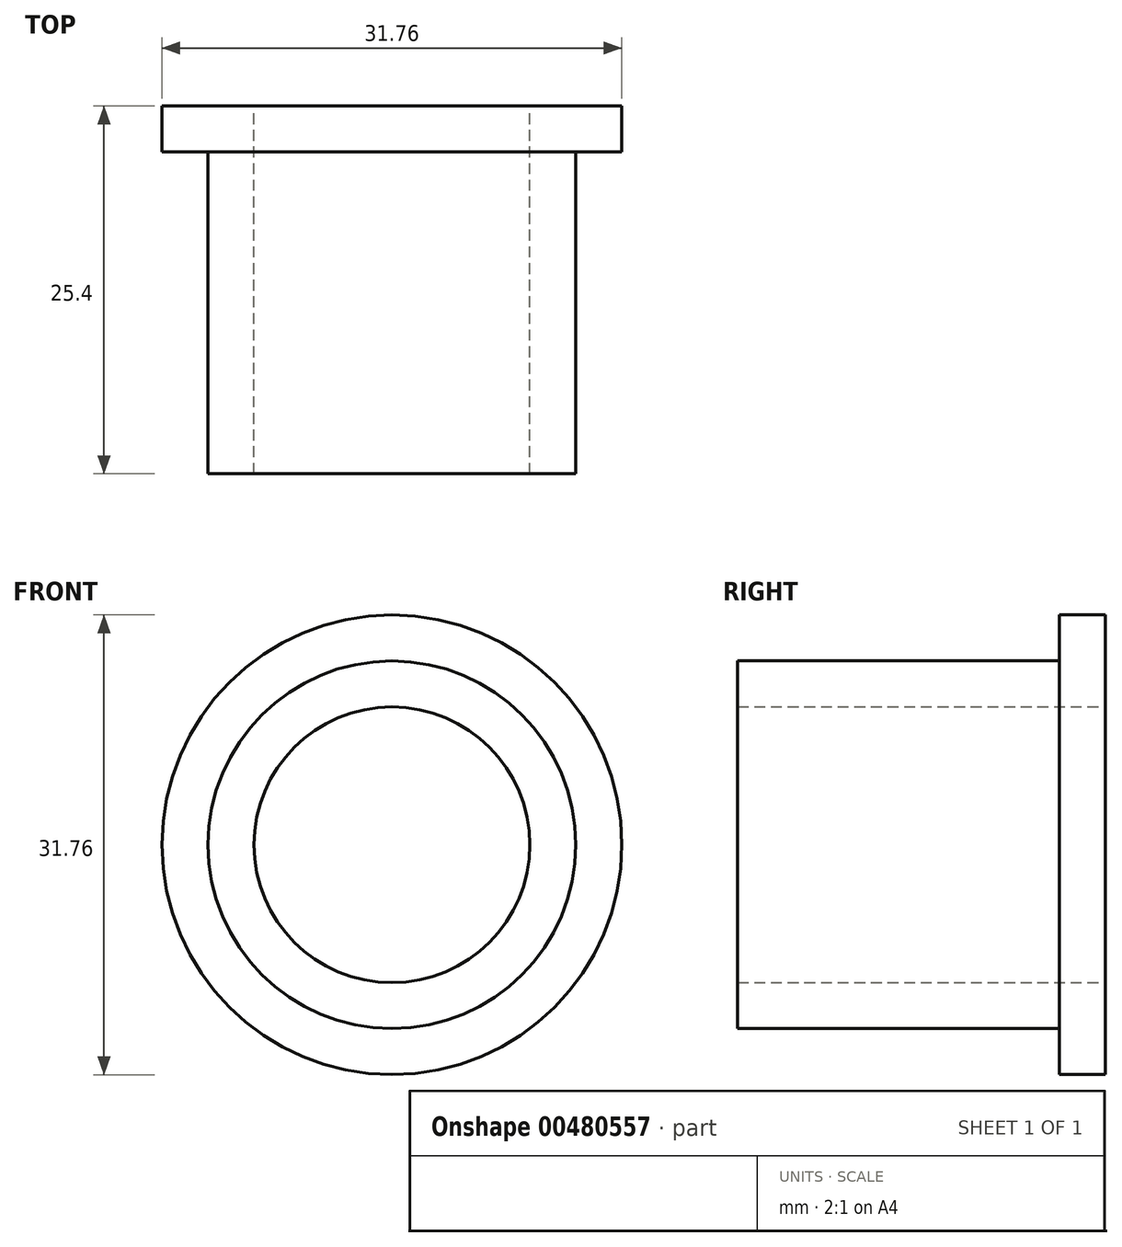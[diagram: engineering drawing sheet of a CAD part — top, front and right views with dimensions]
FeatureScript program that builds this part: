
annotation { "Feature Type Name" : "Feature", "Feature Type Description" : "" }
export const myFeature = defineFeature(function(context is Context, id is Id, definition is map)
    precondition{}
    {
        {
            var Q0;
            Q0=qCreatedBy(makeId("Front.planeOp"),FACE);
            var sketch = newSketch(context, id + "F0", { "sketchPlane" : qUnion([Q0])});
            skCircle(sketch, "E0", {"center": v(0, 0) * mm, "radius": 15.88 * mm});
            skSolve(sketch);
        }
        {
            var Q0;
            Q0=qCreatedBy(makeId("Front.planeOp"),FACE);
            var sketch = newSketch(context, id + "F1", { "sketchPlane" : qUnion([Q0])});
            skCircle(sketch, "E1", {"center": v(0, 0) * mm, "radius": 12.7 * mm});
            skSolve(sketch);
        }
        {
            var Q0;
            Q0=qCreatedBy(makeId("Front.planeOp"),FACE);
            var sketch = newSketch(context, id + "F2", { "sketchPlane" : qUnion([Q0])});
            skCircle(sketch, "E2", {"center": v(0, 0) * mm, "radius": 9.53 * mm});
            skSolve(sketch);
        }
        {
            var Q0;
            Q0 = qSketchRegion(id + "F0", true);
            extrude(context, id + "F3", {"entities" : qUnion([Q0]), "depth" : 3.17 * mm});
        }
        {
            var Q0;
            Q0 = qSketchRegion(id + "F1", true);
            extrude(context, id + "F4", {"entities" : qUnion([Q0]), "operationType" : NewBodyOperationType.ADD, "depth" : 25.4 * mm});
        }
        {
            var Q0;
            Q0 = qSketchRegion(id + "F2", true);
            extrude(context, id + "F5", {"entities" : qUnion([Q0]), "operationType" : NewBodyOperationType.REMOVE, "depth" : 25.4 * mm});
        }
    });
